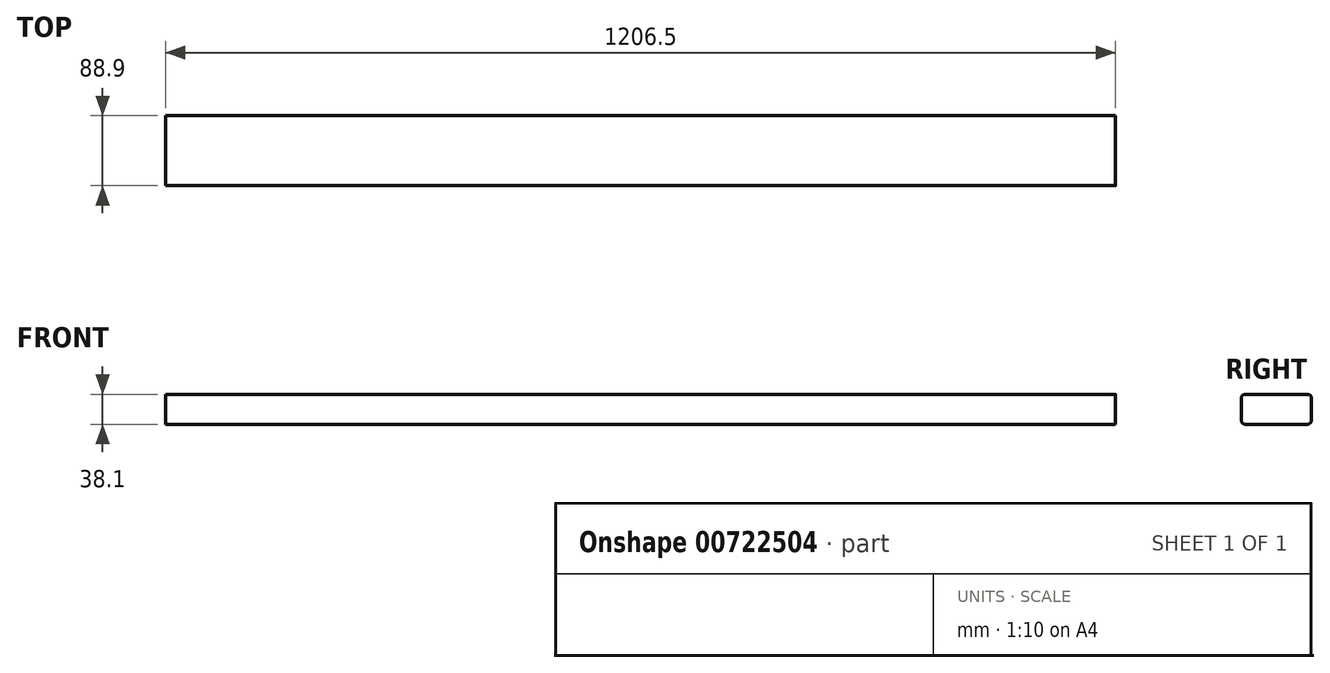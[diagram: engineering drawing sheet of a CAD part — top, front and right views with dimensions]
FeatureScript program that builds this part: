
annotation { "Feature Type Name" : "Feature", "Feature Type Description" : "" }
export const myFeature = defineFeature(function(context is Context, id is Id, definition is map)
    precondition{}
    {
        {
            var Q0;
            Q0=qCreatedBy(makeId("Top.planeOp"),FACE);
            var sketch = newSketch(context, id + "F0", { "sketchPlane" : qUnion([Q0])});
            skLineSegment(sketch, "E0", {"start": v(0, 0) * mm, "end": v(1206.5, 0) * mm});
            skLineSegment(sketch, "E1", {"start": v(1206.5, 0) * mm, "end": v(1206.5, -88.9) * mm});
            skLineSegment(sketch, "E2", {"start": v(1206.5, -88.9) * mm, "end": v(0, -88.9) * mm});
            skLineSegment(sketch, "E3", {"start": v(0, -88.9) * mm, "end": v(0, 0) * mm});
            skSolve(sketch);
        }
        {
            var Q0;
            Q0=makeQuery(id+"F0.imprint","IMPRINT",FACE,{"disambiguationData":[TD([[makeQuery(id+"F0.imprint","IMPRINT",EDGE,{"derivedFrom":sQuery(id+"F0.wireOp",EDGE,"E0")}),-1.0]])]});
            extrude(context, id + "F1", {"entities" : qUnion([Q0]), "depth" : 38.1 * mm, "offsetDistance" : 25.4 * mm});
        }
        {
            var Q0;
            Q0=makeQuery(id+"F1.opExtrude","CAP_EDGE",EDGE,{"disambiguationData":[OSD([sQuery(id+"F0.wireOp",EDGE,"E2")])],"isStart":false});
            var Q1;
            Q1=makeQuery(id+"F1.opExtrude","CAP_EDGE",EDGE,{"disambiguationData":[OSD([sQuery(id+"F0.wireOp",EDGE,"E2")])],"isStart":true});
            var Q2;
            Q2=makeQuery(id+"F1.opExtrude","CAP_EDGE",EDGE,{"disambiguationData":[OSD([sQuery(id+"F0.wireOp",EDGE,"E0")])],"isStart":false});
            var Q3;
            Q3=makeQuery(id+"F1.opExtrude","CAP_EDGE",EDGE,{"disambiguationData":[OSD([sQuery(id+"F0.wireOp",EDGE,"E0")])],"isStart":true});
            fillet(context, id + "F2", {"entities" : qUnion([Q0, Q1, Q2, Q3]), "radius" : 5.08 * mm, "tangentPropagation" : true, "allowEdgeOverflow" : false});
        }
    });
